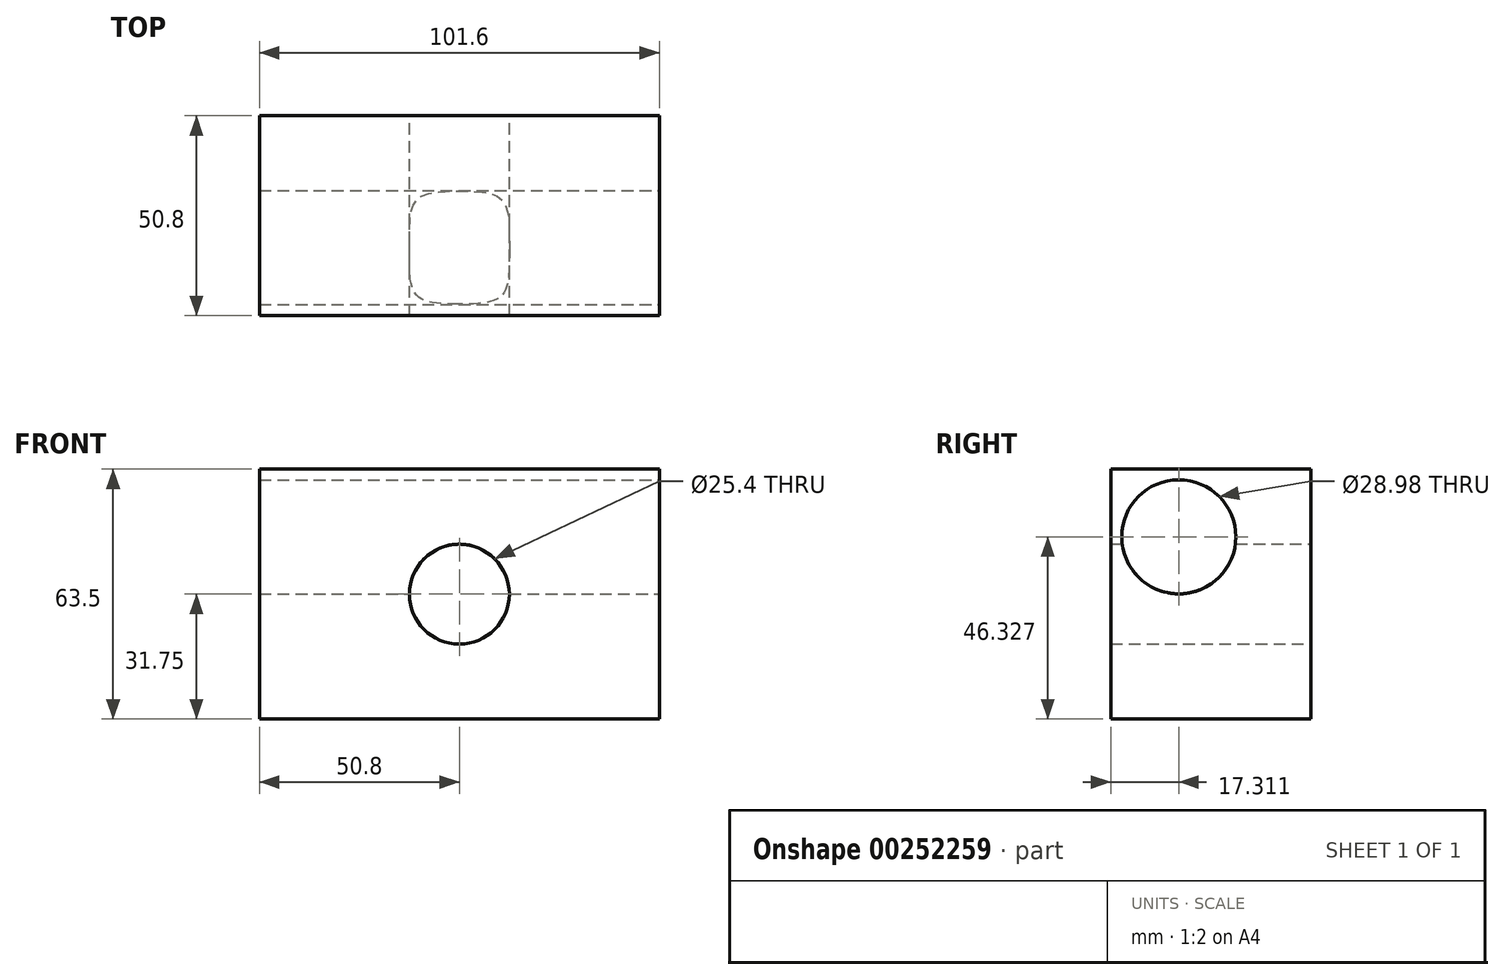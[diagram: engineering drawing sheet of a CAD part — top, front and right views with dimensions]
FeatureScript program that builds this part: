
annotation { "Feature Type Name" : "Feature", "Feature Type Description" : "" }
export const myFeature = defineFeature(function(context is Context, id is Id, definition is map)
    precondition{}
    {
        {
            var Q0;
            Q0=qCreatedBy(makeId("Front.planeOp"),FACE);
            var sketch = newSketch(context, id + "F0", { "sketchPlane" : qUnion([Q0])});
            skLineSegment(sketch, "E0.bottom", {"start": v(50.8, -31.75) * mm, "end": v(-50.8, -31.75) * mm});
            skLineSegment(sketch, "E0.top", {"start": v(50.8, 31.75) * mm, "end": v(-50.8, 31.75) * mm});
            skLineSegment(sketch, "E0.left", {"start": v(50.8, -31.75) * mm, "end": v(50.8, 31.75) * mm});
            skLineSegment(sketch, "E0.right", {"start": v(-50.8, -31.75) * mm, "end": v(-50.8, 31.75) * mm});
            skPoint(sketch, "E0.middle", {"position": v(0, 0) * mm});
            skCircle(sketch, "E1", {"center": v(0, 0) * mm, "radius": 12.7 * mm});
            skSolve(sketch);
        }
        {
            var Q0;
            Q0 = qSketchRegion(id + "F0", true);
            extrude(context, id + "F1", {"entities" : qUnion([Q0]), "depth" : 50.8 * mm});
        }
        {
            var Q0;
            Q0=makeQuery(id+"F1.opExtrude","SWEPT_FACE",FACE,{"disambiguationData":[OSD([sQuery(id+"F0.wireOp",EDGE,"E0.left")])]});
            var sketch = newSketch(context, id + "F2", { "sketchPlane" : qUnion([Q0])});
            skCircle(sketch, "E2", {"center": v(-33.49, 14.58) * mm, "radius": 14.5 * mm});
            skSolve(sketch);
        }
        {
            var Q0;
            Q0=makeQuery(id+"F2.imprint","IMPRINT",FACE,{"disambiguationData":[TD([[makeQuery(id+"F2.imprint","IMPRINT",EDGE,{"derivedFrom":sQuery(id+"F2.wireOp",EDGE,"E2")}),1.0]])]});
            extrude(context, id + "F3", {"entities" : qUnion([Q0]), "operationType" : NewBodyOperationType.REMOVE, "endBound" : BoundingType.THROUGH_ALL, "oppositeDirection" : true, "depth" : 25.4 * mm});
        }
    });
